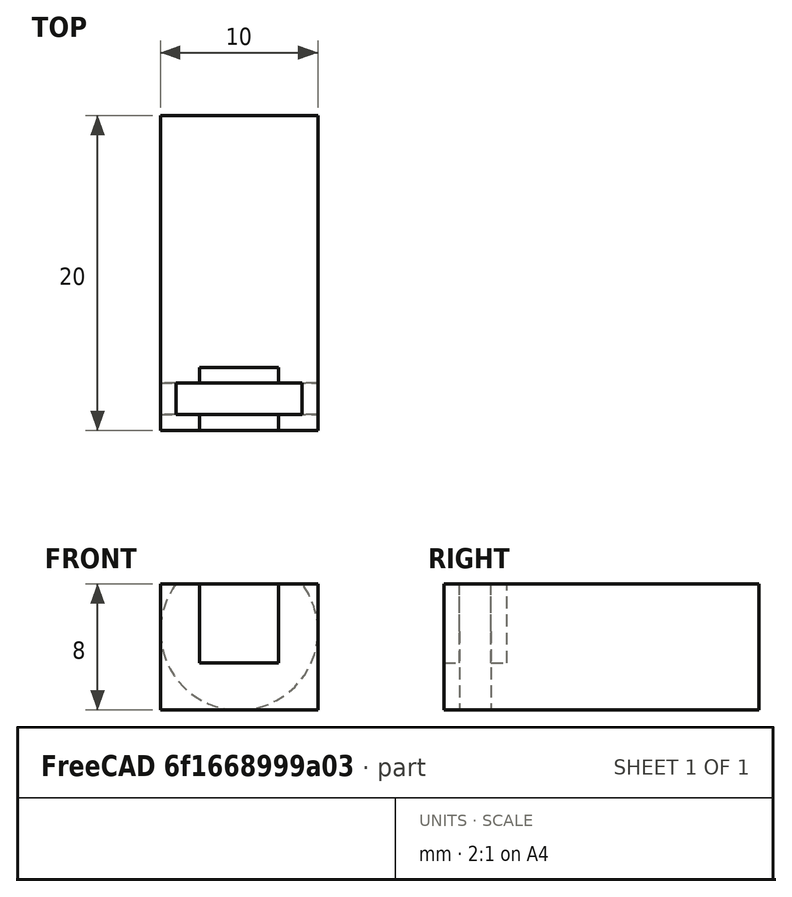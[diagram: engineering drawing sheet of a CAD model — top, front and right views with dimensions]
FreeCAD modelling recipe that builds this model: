
FCSTD DOCUMENT  (FreeCAD 0.16R4924 (Git))
Label: pin_v2
License: All rights reserved
LicenseURL: http://en.wikipedia.org/wiki/All_rights_reserved
objects: Part::Box×3, Part::Cut×3, Part::Cylinder×1
note: 7 computed .brp shape members not serialized (recipe doc carries the construction recipe); baked Part::Feature solids carry a one-line shape summary decoded from their .brp

FEATURE [Part::Box] Box  label="pin"
  Height = 8
  Length = 10
  Width = 20
FEATURE [Part::Cylinder] Cylinder  label="solenoid_head_slot"
  Angle = 360
  Height = 2
  Placement = pos=(5,3,5) rot=(1,0,0;1.5708rad)
  Radius = 5
FEATURE [Part::Cut] Cut
  Base = -> Box
  Tool = -> Cylinder
FEATURE [Part::Box] Box001  label="end_opening"
  Height = 5
  Length = 5
  Placement = pos=(2.5,0,3) rot=(0,0,1;0rad)
  Width = 1
FEATURE [Part::Cut] Cut001
  Base = -> Cut
  Tool = -> Box001
FEATURE [Part::Box] Box002  label="interior_opening"
  Height = 5
  Length = 5
  Placement = pos=(2.5,3,3) rot=(0,0,1;0rad)
  Width = 1
FEATURE [Part::Cut] Cut002
  Base = -> Cut001
  Tool = -> Box002
